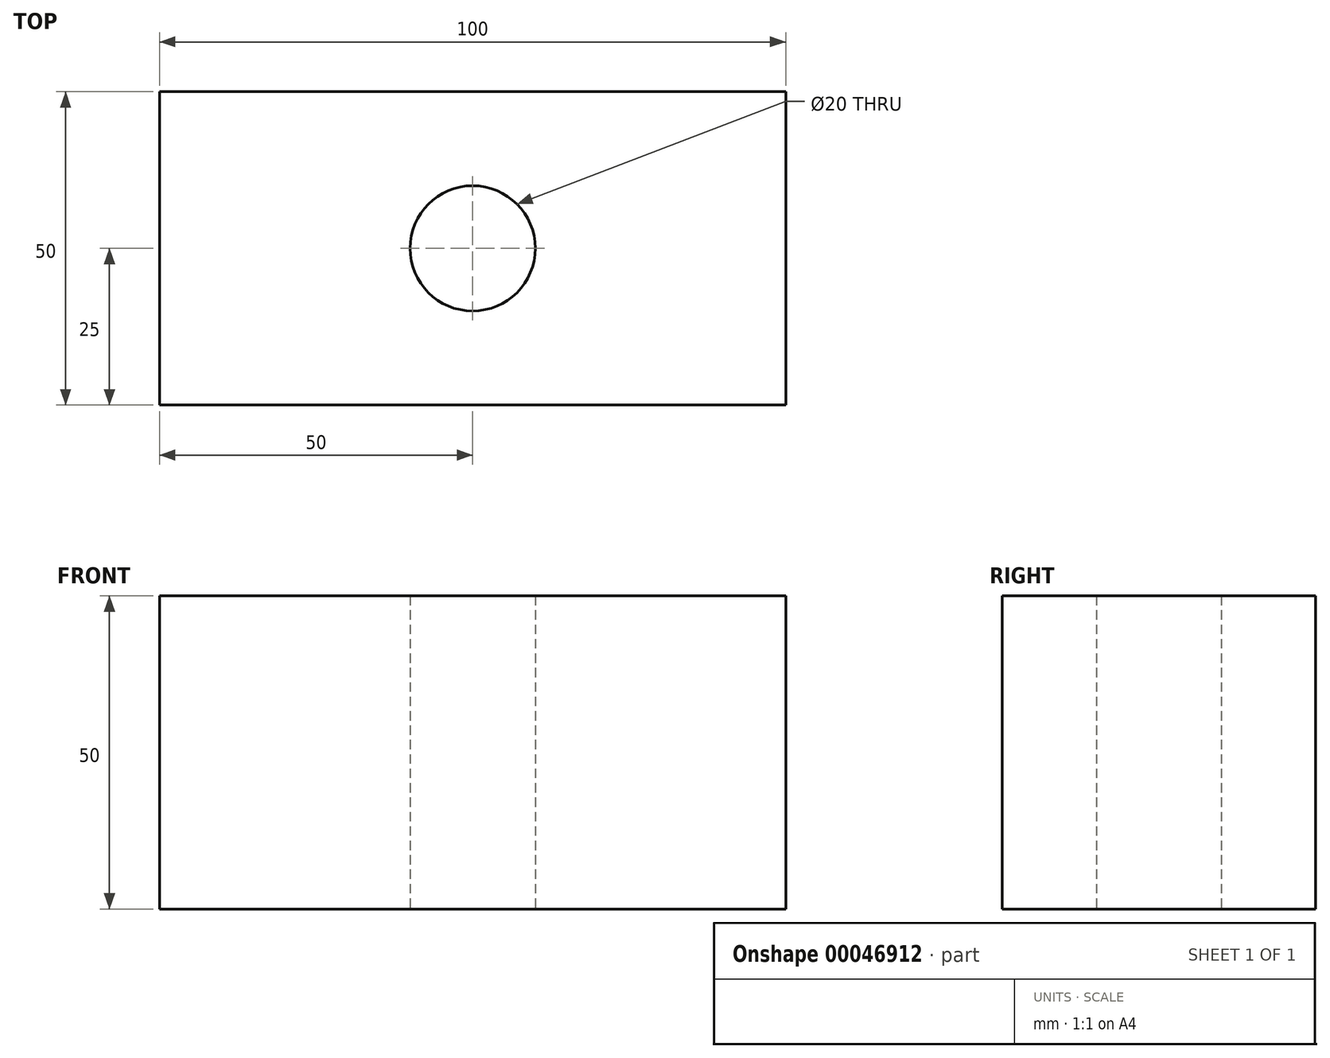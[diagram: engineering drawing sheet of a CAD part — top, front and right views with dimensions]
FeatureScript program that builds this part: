
annotation { "Feature Type Name" : "Feature", "Feature Type Description" : "" }
export const myFeature = defineFeature(function(context is Context, id is Id, definition is map)
    precondition{}
    {
        {
            var Q0;
            Q0=qCreatedBy(makeId("Top.planeOp"),FACE);
            var sketch = newSketch(context, id + "F0", { "sketchPlane" : qUnion([Q0])});
            skLineSegment(sketch, "E0.rect.bottom", {"start": v(-50, -25) * mm, "end": v(50, -25) * mm});
            skLineSegment(sketch, "E0.rect.top", {"start": v(-50, 25) * mm, "end": v(50, 25) * mm});
            skLineSegment(sketch, "E0.rect.left", {"start": v(-50, -25) * mm, "end": v(-50, 25) * mm});
            skLineSegment(sketch, "E0.rect.right", {"start": v(50, -25) * mm, "end": v(50, 25) * mm});
            skPoint(sketch, "E0.rect.middle", {"position": v(0, 0) * mm});
            skCircle(sketch, "E1", {"center": v(0, 0) * mm, "radius": 10 * mm});
            skSolve(sketch);
        }
        {
            var Q0;
            Q0=makeQuery(id+"F0.imprint","IMPRINT",FACE,{"disambiguationData":[TD([[makeQuery(id+"F0.imprint","IMPRINT",EDGE,{"derivedFrom":sQuery(id+"F0.wireOp",EDGE,"E0.rect.bottom")}),1.0]])]});
            extrude(context, id + "F1", {"entities" : qUnion([Q0]), "depth" : 50 * mm});
        }
    });
